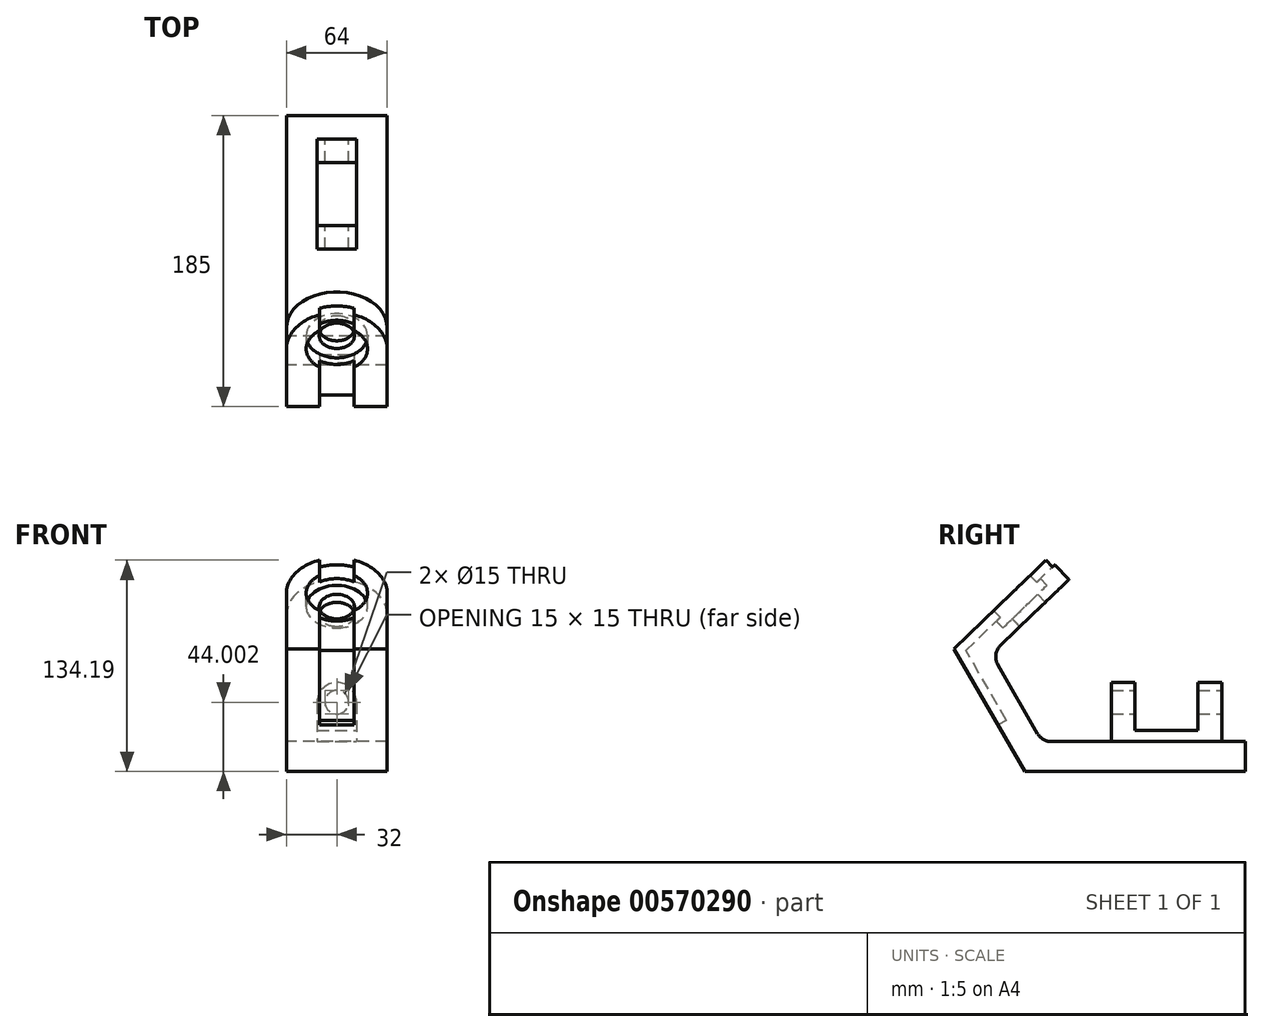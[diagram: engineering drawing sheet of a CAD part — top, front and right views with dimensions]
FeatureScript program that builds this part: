
annotation { "Feature Type Name" : "Feature", "Feature Type Description" : "" }
export const myFeature = defineFeature(function(context is Context, id is Id, definition is map)
    precondition{}
    {
        {
            var Q0;
            Q0=qCreatedBy(makeId("Right.planeOp"),FACE);
            var sketch = newSketch(context, id + "F0", { "sketchPlane" : qUnion([Q0])});
            skLineSegment(sketch, "E0", {"start": v(85.81, -31.82) * mm, "end": v(-54.19, -31.82) * mm});
            skLineSegment(sketch, "E1", {"start": v(-54.19, -31.82) * mm, "end": v(-99.19, 46.12) * mm});
            skLineSegment(sketch, "E2", {"start": v(-99.19, 46.12) * mm, "end": v(-62.47, 81.52) * mm});
            skLineSegment(sketch, "E3", {"start": v(-62.47, 81.52) * mm, "end": v(-49.28, 67.83) * mm});
            skLineSegment(sketch, "E4", {"start": v(-49.28, 67.83) * mm, "end": v(-69.67, 48.18) * mm});
            skLineSegment(sketch, "E5", {"start": v(-71.4, 35.98) * mm, "end": v(-46.1, -7.82) * mm});
            skLineSegment(sketch, "E6", {"start": v(-37.44, -12.82) * mm, "end": v(85.81, -12.82) * mm});
            skLineSegment(sketch, "E7", {"start": v(85.81, -12.82) * mm, "end": v(85.81, -31.82) * mm});
            skPoint(sketch, "E8.visualSharp", {"position": v(-43.22, -12.82) * mm});
            skArc(sketch, "E8.filletArc", {"start": v(-46.1, -7.82) * mm, "mid": v(-42.44, -11.48) * mm, "end": v(-37.44, -12.82) * mm});
            skPoint(sketch, "E9.visualSharp", {"position": v(-75.3, 42.76) * mm});
            skArc(sketch, "E9.filletArc", {"start": v(-69.67, 48.18) * mm, "mid": v(-72.63, 42.38) * mm, "end": v(-71.4, 35.98) * mm});
            skSolve(sketch);
        }
        {
            var Q0;
            Q0 = qSketchRegion(id + "F0", true);
            extrude(context, id + "F1", {"entities" : qUnion([Q0]), "depth" : 64 * mm, "offsetDistance" : 25 * mm});
        }
        {
            var Q0;
            Q0=makeQuery(id+"F1.opExtrude","SWEPT_FACE",FACE,{"disambiguationData":[OSD([sQuery(id+"F0.wireOp",EDGE,"E1")])]});
            var sketch = newSketch(context, id + "F2", { "sketchPlane" : qUnion([Q0])});
            skLineSegment(sketch, "E10.0", {"start": v(21, 89.54) * mm, "end": v(21, 33.54) * mm});
            skLineSegment(sketch, "E11.0", {"start": v(43, 89.54) * mm, "end": v(43, 33.54) * mm});
            skLineSegment(sketch, "E12", {"start": v(21, 33.54) * mm, "end": v(43, 33.54) * mm});
            skLineSegment(sketch, "E13", {"start": v(21, 89.54) * mm, "end": v(21, 113.33) * mm});
            skLineSegment(sketch, "E14", {"start": v(43, 89.54) * mm, "end": v(43, 113.33) * mm});
            skLineSegment(sketch, "E15", {"start": v(43, 113.33) * mm, "end": v(21, 113.33) * mm});
            skSolve(sketch);
        }
        {
            var Q0;
            Q0=makeQuery(id+"F1.opExtrude","SWEPT_FACE",FACE,{"disambiguationData":[OSD([sQuery(id+"F0.wireOp",EDGE,"E2")])]});
            var sketch = newSketch(context, id + "F3", { "sketchPlane" : qUnion([Q0])});
            skArc(sketch, "E16", {"start": v(64, 11.6) * mm, "mid": v(32, 43.6) * mm, "end": v(0, 11.6) * mm});
            skLineSegment(sketch, "E17", {"start": v(0, 11.6) * mm, "end": v(64, 11.6) * mm});
            skSolve(sketch);
        }
        {
            var Q0;
            Q0=makeQuery(id+"F3.imprint","IMPRINT",FACE,{"disambiguationData":[TD([[makeQuery(id+"F3.imprint","IMPRINT",EDGE,{"derivedFrom":sQuery(id+"F3.wireOp",EDGE,"E16")}),1.0]])]});
            extrude(context, id + "F4", {"entities" : qUnion([Q0]), "operationType" : NewBodyOperationType.ADD, "oppositeDirection" : true, "depth" : 19 * mm, "offsetDistance" : 25 * mm});
        }
        {
            var Q0;
            Q0=makeQuery(id+"F4.boolean.opBoolean","MERGE",FACE,{"derivedFrom":[makeQuery(id+"F1.opExtrude","SWEPT_FACE",FACE,{"disambiguationData":[OSD([sQuery(id+"F0.wireOp",EDGE,"E2")])]}),makeQuery(id+"F4.opExtrude","CAP_FACE",FACE,{"disambiguationData":[OSD([sQuery(id+"F3.wireOp",EDGE,"E16"),sQuery(id+"F3.wireOp",EDGE,"E17")])],"isStart":true})]});
            var sketch = newSketch(context, id + "F5", { "sketchPlane" : qUnion([Q0])});
            skSolve(sketch);
        }
        {
            var Q0;
            Q0 = qSketchRegion(id + "F2", true);
            extrude(context, id + "F6", {"entities" : qUnion([Q0]), "operationType" : NewBodyOperationType.REMOVE, "oppositeDirection" : true, "depth" : 6 * mm, "offsetDistance" : 25 * mm});
        }
        {
            var Q0;
            {var subQ0=sQuery(id+"F0.wireOp",EDGE,"E2");Q0=makeQuery(id+"F5.imprint","IMPRINT",FACE,{"disambiguationData":[TD([[makeQuery(id+"F5.imprint","IMPRINT",EDGE,{"derivedFrom":makeQuery(id+"F1.opExtrude","CAP_EDGE",EDGE,{"disambiguationData":[OSD([subQ0])],"isStart":true})}),-1.0]])]});}
            var sketch = newSketch(context, id + "F7", { "sketchPlane" : qUnion([Q0])});
            skLineSegment(sketch, "E18", {"start": v(21, -39.4) * mm, "end": v(21, 67.05) * mm});
            skLineSegment(sketch, "E19", {"start": v(21, 67.05) * mm, "end": v(43, 67.05) * mm});
            skLineSegment(sketch, "E20", {"start": v(43, 67.05) * mm, "end": v(43, -39.4) * mm});
            skSolve(sketch);
        }
        {
            var Q0;
            {var subQ0=sQuery(id+"F7.wireOp",EDGE,"E18");var subQ3=makeQuery(id+"F5.imprint","IMPRINT",EDGE,{"derivedFrom":makeQuery(id+"F4.opExtrude","CAP_EDGE",EDGE,{"disambiguationData":[OSD([sQuery(id+"F3.wireOp",EDGE,"E16")])],"isStart":true})});var subQ4=makeQuery(id+"F7.imprint","INTERSECT",VERTEX,{"derivedFrom":[subQ3,subQ0]});Q0=makeQuery(id+"F7.imprint","IMPRINT",FACE,{"disambiguationData":[TD([[makeQuery(id+"F7.imprint","IMPRINT",EDGE,{"disambiguationData":[TD([[subQ4,1.0]])],"derivedFrom":subQ3}),1.0]])]});}
            extrude(context, id + "F8", {"entities" : qUnion([Q0]), "operationType" : NewBodyOperationType.REMOVE, "oppositeDirection" : true, "depth" : 6 * mm, "offsetDistance" : 25 * mm});
        }
        {
            var Q0;
            {var subQ0=sQuery(id+"F0.wireOp",EDGE,"E2");Q0=makeQuery(id+"F5.imprint","IMPRINT",FACE,{"disambiguationData":[TD([[makeQuery(id+"F5.imprint","IMPRINT",EDGE,{"derivedFrom":makeQuery(id+"F1.opExtrude","CAP_EDGE",EDGE,{"disambiguationData":[OSD([subQ0])],"isStart":true})}),-1.0]])]});}
            var sketch = newSketch(context, id + "F9", { "sketchPlane" : qUnion([Q0])});
            skCircle(sketch, "E21", {"center": v(32, 11.6) * mm, "radius": 19.5 * mm});
            skSolve(sketch);
        }
        {
            var Q0;
            Q0 = qSketchRegion(id + "F9", true);
            extrude(context, id + "F10", {"entities" : qUnion([Q0]), "operationType" : NewBodyOperationType.REMOVE, "oppositeDirection" : true, "depth" : 12 * mm, "offsetDistance" : 25 * mm});
        }
        {
            var Q0;
            {var subQ0=sQuery(id+"F0.wireOp",EDGE,"E2");Q0=makeQuery(id+"F5.imprint","IMPRINT",FACE,{"disambiguationData":[TD([[makeQuery(id+"F5.imprint","IMPRINT",EDGE,{"derivedFrom":makeQuery(id+"F1.opExtrude","CAP_EDGE",EDGE,{"disambiguationData":[OSD([subQ0])],"isStart":true})}),-1.0]])]});}
            var sketch = newSketch(context, id + "F11", { "sketchPlane" : qUnion([Q0])});
            skCircle(sketch, "E22", {"center": v(32, 11.6) * mm, "radius": 11.19 * mm});
            skSolve(sketch);
        }
        {
            var Q0;
            Q0=makeQuery(id+"F11.imprint","IMPRINT",FACE,{"disambiguationData":[TD([[makeQuery(id+"F11.imprint","IMPRINT",EDGE,{"derivedFrom":sQuery(id+"F11.wireOp",EDGE,"E22")}),1.0]])]});
            var Q1;
            Q1=sQuery(id+"F11.wireOp",EDGE,"E22");
            extrude(context, id + "F12", {"entities" : qUnion([Q0]), "operationType" : NewBodyOperationType.REMOVE, "surfaceEntities" : qUnion([Q1]), "oppositeDirection" : true, "depth" : 25 * mm, "offsetDistance" : 25 * mm});
        }
        {
            var Q0;
            Q0=makeQuery(id+"F1.opExtrude","SWEPT_FACE",FACE,{"disambiguationData":[OSD([sQuery(id+"F0.wireOp",EDGE,"E6")])]});
            var sketch = newSketch(context, id + "F13", { "sketchPlane" : qUnion([Q0])});
            skLineSegment(sketch, "E23", {"start": v(32, 85.81) * mm, "end": v(32, -37.44) * mm});
            skLineSegment(sketch, "E24.bottom", {"start": v(19.5, 70.81) * mm, "end": v(44.5, 70.81) * mm});
            skLineSegment(sketch, "E24.top", {"start": v(19.5, 0.81) * mm, "end": v(44.5, 0.81) * mm});
            skLineSegment(sketch, "E24.left", {"start": v(19.5, 70.81) * mm, "end": v(19.5, 0.81) * mm});
            skLineSegment(sketch, "E24.right", {"start": v(44.5, 70.81) * mm, "end": v(44.5, 0.81) * mm});
            skSolve(sketch);
        }
        {
            var Q0;
            {var subQ5=sQuery(id+"F13.wireOp",EDGE,"E24.left");Q0=makeQuery(id+"F13.imprint","IMPRINT",FACE,{"disambiguationData":[TD([[makeQuery(id+"F13.imprint","IMPRINT",EDGE,{"derivedFrom":subQ5}),1.0]])]});}
            var Q1;
            {var subQ5=sQuery(id+"F13.wireOp",EDGE,"E24.right");Q1=makeQuery(id+"F13.imprint","IMPRINT",FACE,{"disambiguationData":[TD([[makeQuery(id+"F13.imprint","IMPRINT",EDGE,{"derivedFrom":subQ5}),-1.0]])]});}
            extrude(context, id + "F14", {"entities" : qUnion([Q0, Q1]), "operationType" : NewBodyOperationType.ADD, "depth" : 25 * mm, "offsetDistance" : 25 * mm});
        }
        {
            var Q0;
            Q0=makeQuery(id+"F14.opExtrude","SWEPT_FACE",FACE,{"disambiguationData":[OSD([sQuery(id+"F13.wireOp",EDGE,"E24.bottom")])]});
            var sketch = newSketch(context, id + "F15", { "sketchPlane" : qUnion([Q0])});
            skArc(sketch, "E25", {"start": v(-19.5, 12.18) * mm, "mid": v(-32, 24.68) * mm, "end": v(-44.5, 12.18) * mm});
            skLineSegment(sketch, "E26", {"start": v(-44.5, 12.18) * mm, "end": v(-19.5, 12.18) * mm});
            skSolve(sketch);
        }
        {
            var Q0;
            Q0 = qSketchRegion(id + "F15", true);
            var Q1;
            Q1=makeQuery(id+"F14.opExtrude","SWEPT_FACE",FACE,{"disambiguationData":[OSD([sQuery(id+"F13.wireOp",EDGE,"E24.top")])]});
            extrude(context, id + "F16", {"entities" : qUnion([Q0]), "operationType" : NewBodyOperationType.ADD, "endBound" : BoundingType.UP_TO_SURFACE, "oppositeDirection" : true, "depth" : 70 * mm, "endBoundEntityFace" : qUnion([Q1]), "offsetDistance" : 25 * mm});
        }
        {
            var Q0;
            Q0=makeQuery(id+"F16.boolean.opBoolean","MERGE",FACE,{"derivedFrom":[makeQuery(id+"F14.opExtrude","SWEPT_FACE",FACE,{"disambiguationData":[OSD([sQuery(id+"F13.wireOp",EDGE,"E24.bottom")])]}),makeQuery(id+"F16.opExtrude","CAP_FACE",FACE,{"disambiguationData":[OSD([sQuery(id+"F15.wireOp",EDGE,"E25"),sQuery(id+"F15.wireOp",EDGE,"E26")])],"isStart":true})]});
            var sketch = newSketch(context, id + "F17", { "sketchPlane" : qUnion([Q0])});
            skCircle(sketch, "E27", {"center": v(-32, 12.18) * mm, "radius": 7.5 * mm});
            skSolve(sketch);
        }
        {
            var Q0;
            Q0 = qSketchRegion(id + "F17", true);
            var Q1;
            {var subQ0=sQuery(id+"F13.wireOp",EDGE,"E24.top");Q1=makeQuery(id+"F16.boolean.opBoolean","MERGE",FACE,{"derivedFrom":[makeQuery(id+"F14.opExtrude","SWEPT_FACE",FACE,{"disambiguationData":[OSD([subQ0])]}),makeQuery(id+"F16.opExtrude","CAP_FACE",FACE,{"disambiguationData":[OSD([subQ0])],"isStart":false})]});}
            extrude(context, id + "F18", {"entities" : qUnion([Q0]), "operationType" : NewBodyOperationType.REMOVE, "endBound" : BoundingType.UP_TO_SURFACE, "oppositeDirection" : true, "depth" : 25 * mm, "endBoundEntityFace" : qUnion([Q1]), "offsetDistance" : 25 * mm});
        }
        {
            var Q0;
            Q0=makeQuery(id+"F14.opExtrude","SWEPT_FACE",FACE,{"disambiguationData":[OSD([sQuery(id+"F13.wireOp",EDGE,"E24.right")])]});
            var sketch = newSketch(context, id + "F19", { "sketchPlane" : qUnion([Q0])});
            skLineSegment(sketch, "E28.bottom", {"start": v(15.81, 32.76) * mm, "end": v(55.81, 32.76) * mm});
            skLineSegment(sketch, "E28.top", {"start": v(15.81, -5.82) * mm, "end": v(55.81, -5.82) * mm});
            skLineSegment(sketch, "E28.left", {"start": v(15.81, 32.76) * mm, "end": v(15.81, -5.82) * mm});
            skLineSegment(sketch, "E28.right", {"start": v(55.81, 32.76) * mm, "end": v(55.81, -5.82) * mm});
            skSolve(sketch);
        }
        {
            var Q0;
            Q0 = qSketchRegion(id + "F19", true);
            extrude(context, id + "F20", {"entities" : qUnion([Q0]), "operationType" : NewBodyOperationType.REMOVE, "endBound" : BoundingType.THROUGH_ALL, "oppositeDirection" : true, "depth" : 25 * mm, "offsetDistance" : 25 * mm});
        }
    });
